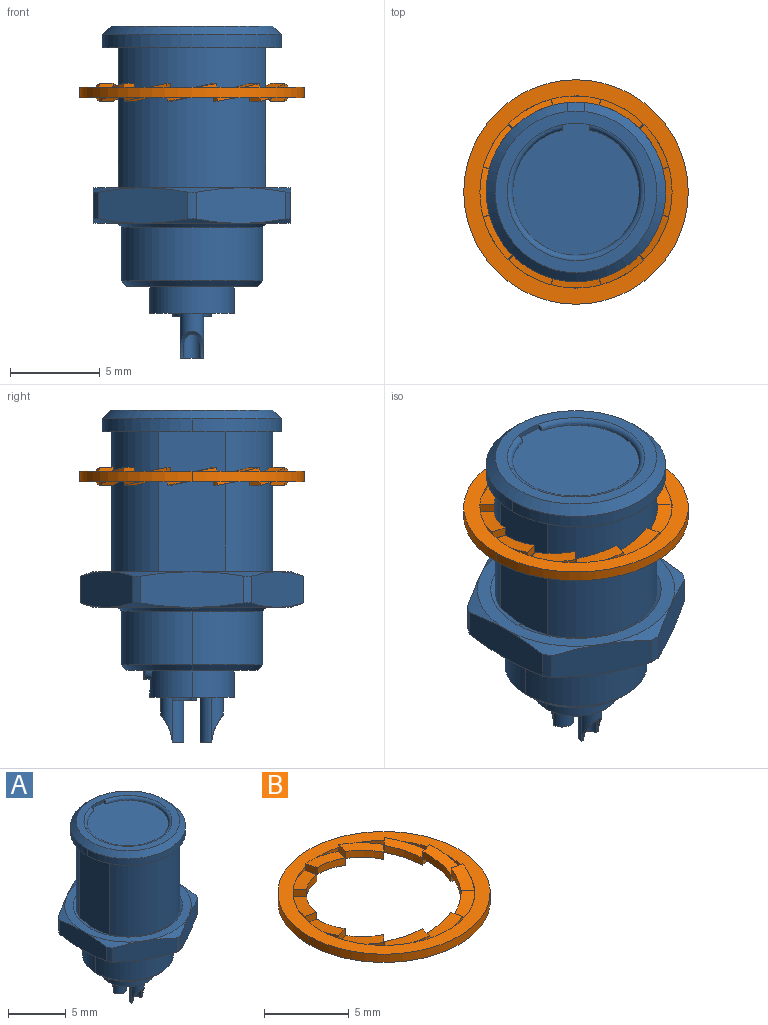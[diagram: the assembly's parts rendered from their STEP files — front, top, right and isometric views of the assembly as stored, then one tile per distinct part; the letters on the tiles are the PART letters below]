
ASSEMBLY  parts=2 mates=2
PART A: 97 faces, bbox 12.6x12.6x18.7 mm
  f0: cylinder r=0.5mm len=2.59mm, axis (0,0,-1), area 4.1mm2, adj f1,f2,f4
  f1: plane 1x1mm, normal (0,0,-1), area 0.8mm2, adj f0,f2
  f2: cylinder r=0.5mm len=2.59mm, axis (0,0,-1), area 2.5mm2, adj f0,f1,f3
  f3: cylinder r=2.5mm len=1.5mm, axis (-1,0,0), area 0.6mm2, adj f2,f4,f6
  f4: plane 1.3x0.65mm, normal (0,0,-1), area 0.3mm2, adj f0,f3,f5
  f5: cylinder r=0.65mm len=2.59mm, axis (0,0,-1), area 5.3mm2, adj f4,f6,f7
  f6: cylinder r=0.65mm len=2.59mm, axis (0,0,-1), area 3mm2, adj f3,f5,f7
  f7: plane 1.71x1.71mm, normal (0,0,-1), area 1mm2, adj f5,f6,f8,f9
  f8: cylinder r=0.85mm len=1.71mm, axis (0,0,1), area 0.3mm2, adj f7,f9,f29
  f9: cylinder r=0.85mm len=1.71mm, axis (0,0,1), area 0.3mm2, adj f7,f8,f29
  f10: cylinder r=0.5mm len=2.59mm, axis (0,0,-1), area 4.1mm2, adj f11,f12,f14
  f11: plane 1x1mm, normal (0,0,-1), area 0.8mm2, adj f10,f12
  f12: cylinder r=0.5mm len=2.59mm, axis (0,0,-1), area 2.5mm2, adj f10,f11,f13
  f13: cylinder r=2.5mm len=1.5mm, axis (1,0,0), area 0.6mm2, adj f12,f14,f16
  f14: plane 1.3x0.65mm, normal (0,0,-1), area 0.3mm2, adj f10,f13,f15
  f15: cylinder r=0.65mm len=2.59mm, axis (0,0,-1), area 5.3mm2, adj f14,f16,f17
  f16: cylinder r=0.65mm len=2.59mm, axis (0,0,-1), area 3mm2, adj f13,f15,f17
  f17: plane 1.71x1.71mm, normal (0,0,-1), area 1mm2, adj f15,f16,f18,f19
  f18: cylinder r=0.85mm len=1.71mm, axis (0,0,1), area 0.3mm2, adj f17,f19,f29
  f19: cylinder r=0.85mm len=1.71mm, axis (0,0,1), area 0.3mm2, adj f17,f18,f29
  f20: plane 0.25x0.2mm, normal (0,1,0), area 0mm2, adj f21,f27,f28,f29
  f21: cone r=1.06mm half-angle=15deg, axis (0,0,1), area 0.3mm2, adj f20,f22,f27,f29
  f22: plane 0.3x0.2mm, normal (0.97,0,-0.26), area 0.1mm2, adj f21,f23,f27,f29
  f23: cylinder r=0.86mm len=0.31mm, axis (0,0,1), area 0.1mm2, adj f22,f24,f27,f29
  f24: plane 0.3x0.2mm, normal (-0.97,0,-0.26), area 0.1mm2, adj f23,f25,f27,f29
  f25: cone r=1.06mm half-angle=15deg, axis (0,0,1), area 0.3mm2, adj f24,f26,f27,f29
  f26: plane 0.25x0.2mm, normal (0,1,0), area 0mm2, adj f25,f27,f28,f29
  f27: plane 2.12x1.35mm, normal (0,0,-1), area 0.7mm2, adj f20,f21,f22,f23,f24,f25,f26,f28
  f28: cylinder r=0.86mm len=1.72mm, axis (0,0,1), area 0.5mm2, adj f20,f26,f27,f29
  f29: plane 4.68x4.68mm, normal (0,0,-1), area 11.8mm2, adj f8,f9,f18,f19,f20,f21,f22,f23
  f30: cylinder r=2.34mm len=4.68mm, axis (0,0,-1), area 13.2mm2, adj f29,f32,f94
  f31: plane 0.38x0.3mm, normal (-1,0,0), area 0.1mm2, adj f32,f94,f95,f96
  f32: cylinder r=2.34mm len=4.68mm, axis (0,0,-1), area 12.2mm2, adj f29,f30,f31,f33,f34,f35,f94,f96
  f33: plane 0.5x0.37mm, normal (0,0,-1), area 0.2mm2, adj f32,f34,f95,f96
  f34: cylinder r=0.5mm len=0.5mm, axis (0,-1,0), area 0.3mm2, adj f32,f33,f35,f95
  f35: plane 0.38x0.3mm, normal (1,0,0), area 0.1mm2, adj f32,f34,f94,f95
  f36: cylinder r=4.5mm len=8.2mm, axis (0,0,1), area 81.9mm2, adj f47,f77,f80,f82
  f37: cylinder r=3.85mm len=1.52mm, axis (0,0,1), area 0.5mm2, adj f38,f40,f41,f42
  f38: plane 0.33x0.32mm, normal (1,0,0), area 0.1mm2, adj f37,f39,f40,f42
  f39: torus R=3.82mm, axis (0,0,-1), area 10mm2, adj f38,f40,f41,f42
  f40: plane 7.35x7.05mm, normal (0,0,1), area 39.5mm2, adj f37,f38,f39,f41
  f41: plane 0.33x0.32mm, normal (-1,0,0), area 0.1mm2, adj f37,f39,f40,f42
  f42: plane 9x9mm, normal (0,0,1), area 17.7mm2, adj f37,f38,f39,f41,f43,f44
  f43: cone r=4.5mm half-angle=45deg, axis (0,0,-1), area 0.7mm2, adj f42,f44,f46
  f44: cone r=4.5mm half-angle=45deg, axis (0,0,-1), area 20.4mm2, adj f42,f43,f45,f46
  f45: cylinder r=5mm len=10mm, axis (0,0,1), area 11mm2, adj f44,f46,f47
  f46: cylinder r=5mm len=10mm, axis (0,0,1), area 11mm2, adj f43,f44,f45,f47
  f47: plane 10x10mm, normal (0,0,-1), area 16.9mm2, adj f36,f45,f46,f48,f80,f82
  f48: cylinder r=4.5mm len=8.2mm, axis (0,0,1), area 81.9mm2, adj f47,f50,f80,f82
  f49: cylinder r=4.22mm len=2.04mm, axis (0,0,-1), area 2.9mm2, adj f50,f77,f79,f80,f81
  f50: cone r=4.22mm half-angle=60deg, axis (0,0,1), area 5mm2, adj f48,f49,f76,f77,f78,f80,f82
  f51: cone r=5.5mm half-angle=70deg, axis (0,0,-1), area 1.7mm2, adj f61,f63,f64,f76
  f52: cone r=5.5mm half-angle=70deg, axis (0,0,-1), area 1.7mm2, adj f58,f60,f61,f76
  f53: plane 11x11mm, normal (0,0,-1), area 24.3mm2, adj f56,f59,f62,f65,f69,f73,f79,f81
  f54: cone r=5.5mm half-angle=70deg, axis (0,0,-1), area 1.7mm2, adj f55,f57,f58,f76
  f55: plane 4.96x2.86mm, normal (-0.5,-0.87,0), area 10.5mm2, adj f54,f56,f57,f73,f74,f75
  f56: cone r=5.5mm half-angle=70deg, axis (0,0,1), area 1.7mm2, adj f53,f55,f57,f58
  f57: cylinder r=6.2mm len=1.49mm, axis (0,0,1), area 0.8mm2, adj f54,f55,f56,f58
  f58: plane 5.72x2mm, normal (-1,0,0), area 10.5mm2, adj f52,f54,f56,f57,f59,f60
  f59: cone r=5.5mm half-angle=70deg, axis (0,0,1), area 1.7mm2, adj f53,f58,f60,f61
  f60: cylinder r=6.2mm len=1.49mm, axis (0,0,1), area 0.8mm2, adj f52,f58,f59,f61
  f61: plane 4.96x2.86mm, normal (-0.5,0.87,0), area 10.5mm2, adj f51,f52,f59,f60,f62,f63
  f62: cone r=5.5mm half-angle=70deg, axis (0,0,1), area 1.7mm2, adj f53,f61,f63,f64
  f63: cylinder r=6.2mm len=1.49mm, axis (0,0,1), area 0.8mm2, adj f51,f61,f62,f64
  f64: plane 4.96x2.86mm, normal (0.5,0.87,0), area 10.5mm2, adj f51,f62,f63,f65,f66,f67
  f65: cone r=5.5mm half-angle=70deg, axis (0,0,1), area 1.7mm2, adj f53,f64,f66,f68
  f66: cylinder r=6.2mm len=1.49mm, axis (0,0,1), area 0.8mm2, adj f64,f65,f67,f68
  f67: cone r=5.5mm half-angle=70deg, axis (0,0,-1), area 1.7mm2, adj f64,f66,f68,f76
  f68: plane 5.72x2mm, normal (1,0,0), area 10.5mm2, adj f65,f66,f67,f69,f70,f71
  f69: cone r=5.5mm half-angle=70deg, axis (0,0,1), area 1.7mm2, adj f53,f68,f70,f72
  f70: cylinder r=6.2mm len=1.49mm, axis (0,0,1), area 0.8mm2, adj f68,f69,f71,f72
  f71: cone r=5.5mm half-angle=70deg, axis (0,0,-1), area 1.7mm2, adj f68,f70,f72,f76
  f72: plane 4.96x2.86mm, normal (0.5,-0.87,0), area 10.5mm2, adj f69,f70,f71,f73,f74,f75
  f73: cone r=5.5mm half-angle=70deg, axis (0,0,1), area 1.7mm2, adj f53,f55,f72,f74
  f74: cylinder r=6.2mm len=1.49mm, axis (0,0,1), area 0.8mm2, adj f55,f72,f73,f75
  f75: cone r=5.5mm half-angle=70deg, axis (0,0,-1), area 1.7mm2, adj f55,f72,f74,f76
  f76: plane 11x11mm, normal (0,0,1), area 24.3mm2, adj f50,f51,f52,f54,f67,f71,f75,f77
  f77: cone r=4.22mm half-angle=60deg, axis (0,0,1), area 5mm2, adj f36,f49,f50,f76,f78,f80,f82
  f78: cylinder r=4.22mm len=2.04mm, axis (0,0,-1), area 2.9mm2, adj f50,f77,f79,f81,f82
  f79: cone r=4.22mm half-angle=60deg, axis (0,0,-1), area 6.7mm2, adj f49,f53,f78,f80,f81,f82,f83
  f80: plane 10.04x3.9mm, normal (1,0,0), area 33.5mm2, adj f36,f47,f48,f49,f50,f77,f79,f81
  f81: cone r=4.22mm half-angle=60deg, axis (0,0,-1), area 6.7mm2, adj f49,f53,f78,f79,f80,f82,f84
  f82: plane 10.04x3.9mm, normal (-1,0,0), area 33.5mm2, adj f36,f47,f48,f50,f77,f78,f79,f81
  f83: cone r=3.95mm half-angle=45deg, axis (0,0,1), area 7.1mm2, adj f79,f80,f82,f84,f86
  f84: cone r=3.95mm half-angle=45deg, axis (0,0,1), area 7.1mm2, adj f80,f81,f82,f83,f85
  f85: cylinder r=3.95mm len=7.9mm, axis (0,0,1), area 37.2mm2, adj f84,f86,f88
  f86: cylinder r=3.95mm len=7.9mm, axis (0,0,1), area 37.2mm2, adj f83,f85,f87
  f87: cone r=3.65mm half-angle=45deg, axis (0,0,1), area 5.1mm2, adj f86,f88,f89
  f88: cone r=3.65mm half-angle=45deg, axis (0,0,1), area 5.1mm2, adj f85,f87,f89
  f89: plane 7.3x7.3mm, normal (0,0,-1), area 23.2mm2, adj f87,f88,f90,f91,f92,f93
  f90: plane 0.37x0.3mm, normal (1,0,0), area 0.1mm2, adj f89,f91,f93,f94
  f91: cylinder r=2.4mm len=4.8mm, axis (0,0,1), area 4.1mm2, adj f89,f90,f92,f94
  f92: plane 0.37x0.3mm, normal (-1,0,0), area 0.1mm2, adj f89,f91,f93,f94
  f93: cylinder r=2.75mm len=1.52mm, axis (0,0,1), area 0.5mm2, adj f89,f90,f92,f94
  f94: plane 5.15x4.8mm, normal (0,0,-1), area 0.9mm2, adj f30,f31,f32,f35,f90,f91,f92,f93
  f95: cylinder r=2.7mm len=1.5mm, axis (0,0,1), area 1.1mm2, adj f31,f33,f34,f35,f94,f96
  f96: cylinder r=0.5mm len=0.5mm, axis (0,1,0), area 0.3mm2, adj f31,f32,f33,f95
PART B: 100 faces, bbox 12.5x12.5x1 mm
  f0: bspline ~2.72x2.12mm, area 2mm2, adj f1,f2,f82,f83,f84
  f1: cylinder r=5.35mm len=0.87mm, axis (0,0,-1), area 0.1mm2, adj f0,f2,f92
  f2: plane 0.57x0.56mm, normal (-0.7,0.71,0), area 0.4mm2, adj f0,f1,f79,f81,f82
  f3: bspline ~2.72x2.12mm, area 2mm2, adj f4,f5,f77,f78,f79
  f4: cylinder r=5.35mm len=1.05mm, axis (0,0,-1), area 0.1mm2, adj f3,f5,f92
  f5: plane 0.77x0.51mm, normal (-0.25,0.97,0), area 0.4mm2, adj f3,f4,f74,f76,f77
  f6: bspline ~2.85x0.95mm, area 2.1mm2, adj f7,f8,f72,f73,f74
  f7: cylinder r=5.35mm len=1.11mm, axis (0,0,-1), area 0.1mm2, adj f6,f8,f92
  f8: plane 0.77x0.51mm, normal (0.27,0.96,0), area 0.4mm2, adj f6,f7,f69,f71,f72
  f9: bspline ~2.72x2.12mm, area 2mm2, adj f10,f11,f67,f68,f69
  f10: cylinder r=5.35mm len=0.87mm, axis (0,0,-1), area 0.1mm2, adj f9,f11,f92
  f11: plane 0.57x0.56mm, normal (0.71,0.7,0), area 0.4mm2, adj f9,f10,f64,f66,f67
  f12: bspline ~2.72x2.12mm, area 2mm2, adj f13,f14,f62,f63,f64
  f13: cylinder r=5.35mm len=1.05mm, axis (0,0,-1), area 0.1mm2, adj f12,f14,f92
  f14: plane 0.77x0.51mm, normal (0.97,0.25,0), area 0.4mm2, adj f12,f13,f59,f61,f62
  f15: bspline ~2.85x0.95mm, area 2mm2, adj f16,f17,f57,f58,f59
  f16: cylinder r=5.35mm len=1.11mm, axis (0,0,-1), area 0.1mm2, adj f15,f17,f92
  f17: plane 0.77x0.51mm, normal (0.96,-0.27,0), area 0.4mm2, adj f15,f16,f54,f56,f57
  f18: bspline ~2.72x2.12mm, area 2mm2, adj f19,f20,f52,f53,f54
  f19: cylinder r=5.35mm len=0.87mm, axis (0,0,-1), area 0.1mm2, adj f18,f20,f92
  f20: plane 0.57x0.56mm, normal (0.7,-0.71,0), area 0.4mm2, adj f18,f19,f49,f51,f52
  f21: bspline ~2.72x2.12mm, area 2mm2, adj f22,f23,f47,f48,f49
  f22: cylinder r=5.35mm len=1.05mm, axis (0,0,-1), area 0.1mm2, adj f21,f23,f92
  f23: plane 0.77x0.51mm, normal (0.25,-0.97,0), area 0.4mm2, adj f21,f22,f44,f46,f47
  f24: bspline ~2.85x0.95mm, area 2.1mm2, adj f25,f26,f42,f43,f44
  f25: cylinder r=5.35mm len=1.11mm, axis (0,0,-1), area 0.1mm2, adj f24,f26,f92
  f26: plane 0.77x0.51mm, normal (-0.27,-0.96,0), area 0.4mm2, adj f24,f25,f39,f41,f42
  f27: bspline ~2.72x2.12mm, area 2mm2, adj f28,f29,f37,f38,f39
  f28: cylinder r=5.35mm len=0.87mm, axis (0,0,-1), area 0.1mm2, adj f27,f29,f92
  f29: plane 0.57x0.56mm, normal (-0.71,-0.7,0), area 0.4mm2, adj f27,f28,f34,f36,f37
  f30: cylinder r=5.35mm len=0.87mm, axis (0,0,-1), area 0.1mm2, adj f33,f95,f99
  f31: cylinder r=5.35mm len=1.05mm, axis (0,0,-1), area 0.1mm2, adj f32,f92,f97
  f32: bspline ~2.72x2.12mm, area 2mm2, adj f31,f33,f34,f97,f98
  f33: plane 0.57x0.56mm, normal (0.7,0.71,0), area 0.4mm2, adj f30,f32,f34,f98,f99
  f34: cylinder r=5.35mm len=2.32mm, axis (0,0,1), area 0.5mm2, adj f29,f32,f33,f36,f92,f95
  f35: cylinder r=5.35mm len=1.05mm, axis (0,0,-1), area 0.1mm2, adj f36,f38,f95
  f36: bspline ~2.72x2.12mm, area 2mm2, adj f29,f34,f35,f37,f38
  f37: cylinder r=4.55mm len=2.02mm, axis (0,0,-1), area 1.2mm2, adj f27,f29,f36,f38
  f38: plane 0.77x0.51mm, normal (0.25,0.97,0), area 0.4mm2, adj f27,f35,f36,f37,f39
  f39: cylinder r=5.35mm len=3.17mm, axis (0,0,1), area 0.5mm2, adj f26,f27,f38,f41,f92,f95
  f40: cylinder r=5.35mm len=1.11mm, axis (0,0,-1), area 0.1mm2, adj f41,f43,f95
  f41: bspline ~2.85x0.95mm, area 2.1mm2, adj f26,f39,f40,f42,f43
  f42: cylinder r=4.55mm len=2.33mm, axis (0,0,-1), area 1.2mm2, adj f24,f26,f41,f43
  f43: plane 0.77x0.51mm, normal (-0.27,0.96,0), area 0.4mm2, adj f24,f40,f41,f42,f44
  f44: cylinder r=5.35mm len=3.17mm, axis (0,0,1), area 0.5mm2, adj f23,f24,f43,f46,f92,f95
  f45: cylinder r=5.35mm len=0.87mm, axis (0,0,-1), area 0.1mm2, adj f46,f48,f95
  f46: bspline ~2.72x2.12mm, area 2mm2, adj f23,f44,f45,f47,f48
  f47: cylinder r=4.55mm len=2.02mm, axis (0,0,-1), area 1.2mm2, adj f21,f23,f46,f48
  f48: plane 0.57x0.56mm, normal (-0.71,0.7,0), area 0.4mm2, adj f21,f45,f46,f47,f49
  f49: cylinder r=5.35mm len=2.32mm, axis (0,0,1), area 0.5mm2, adj f20,f21,f48,f51,f92,f95
  f50: cylinder r=5.35mm len=1.05mm, axis (0,0,-1), area 0.1mm2, adj f51,f53,f95
  f51: bspline ~2.72x2.12mm, area 2mm2, adj f20,f49,f50,f52,f53
  f52: cylinder r=4.55mm len=2.02mm, axis (0,0,-1), area 1.2mm2, adj f18,f20,f51,f53
  f53: plane 0.77x0.51mm, normal (-0.97,0.25,0), area 0.4mm2, adj f18,f50,f51,f52,f54
  f54: cylinder r=5.35mm len=3.17mm, axis (0,0,1), area 0.5mm2, adj f17,f18,f53,f56,f92,f95
  f55: cylinder r=5.35mm len=1.11mm, axis (0,0,-1), area 0.1mm2, adj f56,f58,f95
  f56: bspline ~2.85x0.95mm, area 2mm2, adj f17,f54,f55,f57,f58
  f57: cylinder r=4.55mm len=2.33mm, axis (0,0,-1), area 1.2mm2, adj f15,f17,f56,f58
  f58: plane 0.77x0.51mm, normal (-0.96,-0.27,0), area 0.4mm2, adj f15,f55,f56,f57,f59
  f59: cylinder r=5.35mm len=3.17mm, axis (0,0,1), area 0.5mm2, adj f14,f15,f58,f61,f92,f95
  f60: cylinder r=5.35mm len=0.87mm, axis (0,0,-1), area 0.1mm2, adj f61,f63,f95
  f61: bspline ~2.72x2.12mm, area 2mm2, adj f14,f59,f60,f62,f63
  f62: cylinder r=4.55mm len=2.02mm, axis (0,0,-1), area 1.2mm2, adj f12,f14,f61,f63
  f63: plane 0.57x0.56mm, normal (-0.7,-0.71,0), area 0.4mm2, adj f12,f60,f61,f62,f64
  f64: cylinder r=5.35mm len=2.32mm, axis (0,0,1), area 0.5mm2, adj f11,f12,f63,f66,f92,f95
  f65: cylinder r=5.35mm len=1.05mm, axis (0,0,-1), area 0.1mm2, adj f66,f68,f95
  f66: bspline ~2.72x2.12mm, area 2mm2, adj f11,f64,f65,f67,f68
  f67: cylinder r=4.55mm len=2.02mm, axis (0,0,-1), area 1.2mm2, adj f9,f11,f66,f68
  f68: plane 0.77x0.51mm, normal (-0.25,-0.97,0), area 0.4mm2, adj f9,f65,f66,f67,f69
  f69: cylinder r=5.35mm len=3.17mm, axis (0,0,1), area 0.5mm2, adj f8,f9,f68,f71,f92,f95
  f70: cylinder r=5.35mm len=1.11mm, axis (0,0,-1), area 0.1mm2, adj f71,f73,f95
  f71: bspline ~2.85x0.95mm, area 2.1mm2, adj f8,f69,f70,f72,f73
  f72: cylinder r=4.55mm len=2.33mm, axis (0,0,-1), area 1.2mm2, adj f6,f8,f71,f73
  f73: plane 0.77x0.51mm, normal (0.27,-0.96,0), area 0.4mm2, adj f6,f70,f71,f72,f74
  f74: cylinder r=5.35mm len=3.17mm, axis (0,0,1), area 0.5mm2, adj f5,f6,f73,f76,f92,f95
  f75: cylinder r=5.35mm len=0.87mm, axis (0,0,-1), area 0.1mm2, adj f76,f78,f95
  f76: bspline ~2.72x2.12mm, area 2mm2, adj f5,f74,f75,f77,f78
  f77: cylinder r=4.55mm len=2.02mm, axis (0,0,-1), area 1.2mm2, adj f3,f5,f76,f78
  f78: plane 0.57x0.56mm, normal (0.71,-0.7,0), area 0.4mm2, adj f3,f75,f76,f77,f79
  f79: cylinder r=5.35mm len=2.32mm, axis (0,0,1), area 0.5mm2, adj f2,f3,f78,f81,f92,f95
  f80: cylinder r=5.35mm len=1.05mm, axis (0,0,-1), area 0.1mm2, adj f81,f83,f95
  f81: bspline ~2.72x2.12mm, area 2mm2, adj f2,f79,f80,f82,f83
  f82: cylinder r=4.55mm len=2.02mm, axis (0,0,-1), area 1.2mm2, adj f0,f2,f81,f83
  f83: plane 0.77x0.51mm, normal (0.97,-0.25,0), area 0.4mm2, adj f0,f80,f81,f82,f84
  f84: cylinder r=5.35mm len=3.17mm, axis (0,0,1), area 0.5mm2, adj f0,f83,f88,f90,f92,f95
  f85: cylinder r=5.35mm len=1.11mm, axis (0,0,-1), area 0.1mm2, adj f87,f88,f95
  f86: bspline ~2.85x0.95mm, area 2mm2, adj f87,f89,f90,f91,f96
  f87: plane 0.77x0.51mm, normal (0.96,0.27,0), area 0.4mm2, adj f85,f86,f88,f89,f96
  f88: bspline ~2.85x0.95mm, area 2mm2, adj f84,f85,f87,f89,f90
  f89: cylinder r=4.55mm len=2.33mm, axis (0,0,-1), area 1.2mm2, adj f86,f87,f88,f90
  f90: plane 0.77x0.51mm, normal (-0.96,0.27,0), area 0.4mm2, adj f84,f86,f88,f89,f91
  f91: cylinder r=5.35mm len=1.11mm, axis (0,0,-1), area 0.1mm2, adj f86,f90,f92
  f92: plane 12.5x12.5mm, normal (0,0,-1), area 32.8mm2, adj f1,f4,f7,f10,f13,f16,f19,f22
  f93: cylinder r=6.25mm len=12.5mm, axis (0,0,-1), area 11.8mm2, adj f92,f94,f95
  f94: cylinder r=6.25mm len=12.5mm, axis (0,0,-1), area 11.8mm2, adj f92,f93,f95
  f95: plane 12.5x12.5mm, normal (0,0,1), area 32.8mm2, adj f30,f34,f35,f39,f40,f44,f45,f49
  f96: cylinder r=5.35mm len=3.17mm, axis (0,0,1), area 0.5mm2, adj f86,f87,f92,f95,f97,f99
  f97: plane 0.77x0.51mm, normal (-0.97,-0.25,0), area 0.4mm2, adj f31,f32,f96,f98,f99
  f98: cylinder r=4.55mm len=2.02mm, axis (0,0,-1), area 1.2mm2, adj f32,f33,f97,f99
  f99: bspline ~2.72x2.12mm, area 2mm2, adj f30,f33,f96,f97,f98
PLACE A at identity
PLACE B t=(0,0,4.8)mm
MATE planar B.f95 <-> A.f30  axis (0,0,1) through (2.9,-4.49,11.1)mm
MATE cylindrical B.f1 <-> A.f30  axis (0,0,-1) through (0,0,10.8)mm
